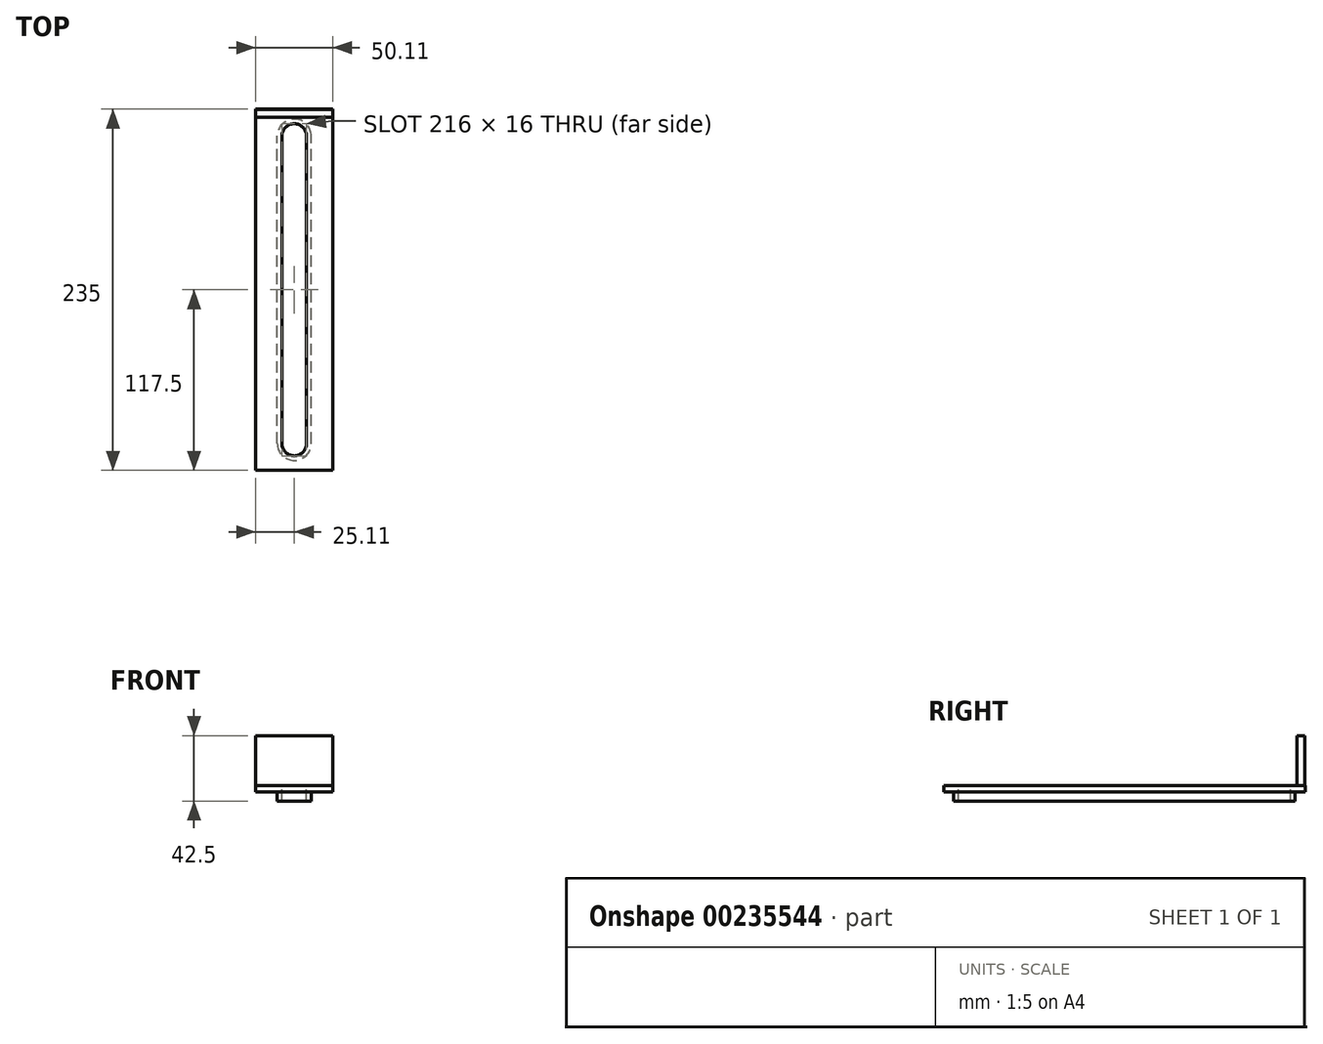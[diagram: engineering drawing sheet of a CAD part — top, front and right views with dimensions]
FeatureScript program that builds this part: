
annotation { "Feature Type Name" : "Feature", "Feature Type Description" : "" }
export const myFeature = defineFeature(function(context is Context, id is Id, definition is map)
    precondition{}
    {
        {
            var Q0;
            Q0=qCreatedBy(makeId("Top.planeOp"),FACE);
            var sketch = newSketch(context, id + "F0", { "sketchPlane" : qUnion([Q0])});
            skLineSegment(sketch, "E0.bottom", {"start": v(25, -117.5) * mm, "end": v(-25, -117.5) * mm});
            skLineSegment(sketch, "E0.top", {"start": v(25, 117.5) * mm, "end": v(-25, 117.5) * mm});
            skLineSegment(sketch, "E0.left", {"start": v(25, -117.5) * mm, "end": v(25, 117.5) * mm});
            skLineSegment(sketch, "E0.right", {"start": v(-25, -117.5) * mm, "end": v(-25, 117.5) * mm});
            skPoint(sketch, "E0.middle", {"position": v(0, 0) * mm});
            skLineSegment(sketch, "E1.left", {"start": v(8, -100) * mm, "end": v(8, 100) * mm});
            skLineSegment(sketch, "E1.right", {"start": v(-8, -100) * mm, "end": v(-8, 100) * mm});
            skArc(sketch, "E2", {"start": v(-8, -100) * mm, "mid": v(0, -108) * mm, "end": v(8, -100) * mm});
            skArc(sketch, "E3", {"start": v(8, 100) * mm, "mid": v(0, 108) * mm, "end": v(-8, 100) * mm});
            skLineSegment(sketch, "E4.left", {"start": v(11, -100) * mm, "end": v(11, 100) * mm});
            skLineSegment(sketch, "E4.right", {"start": v(-11, -100) * mm, "end": v(-11, 100) * mm});
            skArc(sketch, "E5", {"start": v(-11, -100) * mm, "mid": v(0, -111) * mm, "end": v(11, -100) * mm});
            skArc(sketch, "E6", {"start": v(11, 100) * mm, "mid": v(0, 111) * mm, "end": v(-11, 100) * mm});
            skSolve(sketch);
        }
        {
            var Q0;
            Q0 = qSketchRegion(id + "F0", true);
            extrude(context, id + "F1", {"entities" : qUnion([Q0]), "depth" : 4 * mm});
        }
        {
            var Q0;
            Q0=makeQuery(id+"F0.imprint","IMPRINT",FACE,{"disambiguationData":[TD([[makeQuery(id+"F0.imprint","IMPRINT",EDGE,{"derivedFrom":sQuery(id+"F0.wireOp",EDGE,"E1.left")}),-1.0]])]});
            extrude(context, id + "F2", {"entities" : qUnion([Q0]), "operationType" : NewBodyOperationType.ADD, "depth" : 10 * mm});
        }
        {
            var Q0;
            Q0=makeQuery(id+"F1.opExtrude","SWEPT_BODY",BODY,{"disambiguationData":[OSD([sQuery(id+"F0.wireOp",EDGE,"E0.bottom"),sQuery(id+"F0.wireOp",EDGE,"E0.top"),sQuery(id+"F0.wireOp",EDGE,"E0.left"),sQuery(id+"F0.wireOp",EDGE,"E0.right"),sQuery(id+"F0.wireOp",EDGE,"E4.left"),sQuery(id+"F0.wireOp",EDGE,"E4.right"),sQuery(id+"F0.wireOp",EDGE,"E5"),sQuery(id+"F0.wireOp",EDGE,"E6")])]});
            var Q1;
            Q1=sQuery(id+"F0.wireOp",EDGE,"E1.right");
            transform(context, id + "F3", {"entities" : qUnion([Q0]), "transformType" : TransformType.ROTATION, "transformAxis" : qUnion([Q1]), "angle" : 180 * degree, "makeCopy" : false});
        }
        {
            var Q0;
            Q0=makeQuery(id+"F1.opExtrude","SWEPT_BODY",BODY,{"disambiguationData":[OSD([sQuery(id+"F0.wireOp",EDGE,"E0.bottom"),sQuery(id+"F0.wireOp",EDGE,"E0.top"),sQuery(id+"F0.wireOp",EDGE,"E0.left"),sQuery(id+"F0.wireOp",EDGE,"E0.right"),sQuery(id+"F0.wireOp",EDGE,"E4.left"),sQuery(id+"F0.wireOp",EDGE,"E4.right"),sQuery(id+"F0.wireOp",EDGE,"E5"),sQuery(id+"F0.wireOp",EDGE,"E6")])]});
            transform(context, id + "F4", {"entities" : qUnion([Q0]), "transformType" : TransformType.TRANSLATION_3D, "dx" : 16 * mm, "dy" : 0 * mm, "dz" : 0 * mm, "makeCopy" : false});
        }
        {
            var Q0;
            Q0=makeQuery(id+"F0.imprint","IMPRINT",FACE,{"disambiguationData":[TD([[makeQuery(id+"F0.imprint","IMPRINT",EDGE,{"derivedFrom":sQuery(id+"F0.wireOp",EDGE,"E0.bottom")}),-1.0]])]});
            var sketch = newSketch(context, id + "F5", { "sketchPlane" : qUnion([Q0])});
            skLineSegment(sketch, "E7.bottom", {"start": v(-25.1, 117.3) * mm, "end": v(24.9, 117.3) * mm});
            skLineSegment(sketch, "E7.top", {"start": v(-25.1, 112.3) * mm, "end": v(24.9, 112.3) * mm});
            skLineSegment(sketch, "E7.left", {"start": v(-25.1, 117.3) * mm, "end": v(-25.1, 112.3) * mm});
            skLineSegment(sketch, "E7.right", {"start": v(24.9, 117.3) * mm, "end": v(24.9, 112.3) * mm});
            skSolve(sketch);
        }
        {
            var Q0;
            Q0 = qSketchRegion(id + "F5", true);
            extrude(context, id + "F6", {"entities" : qUnion([Q0]), "operationType" : NewBodyOperationType.ADD, "depth" : 32.5 * mm});
        }
    });
